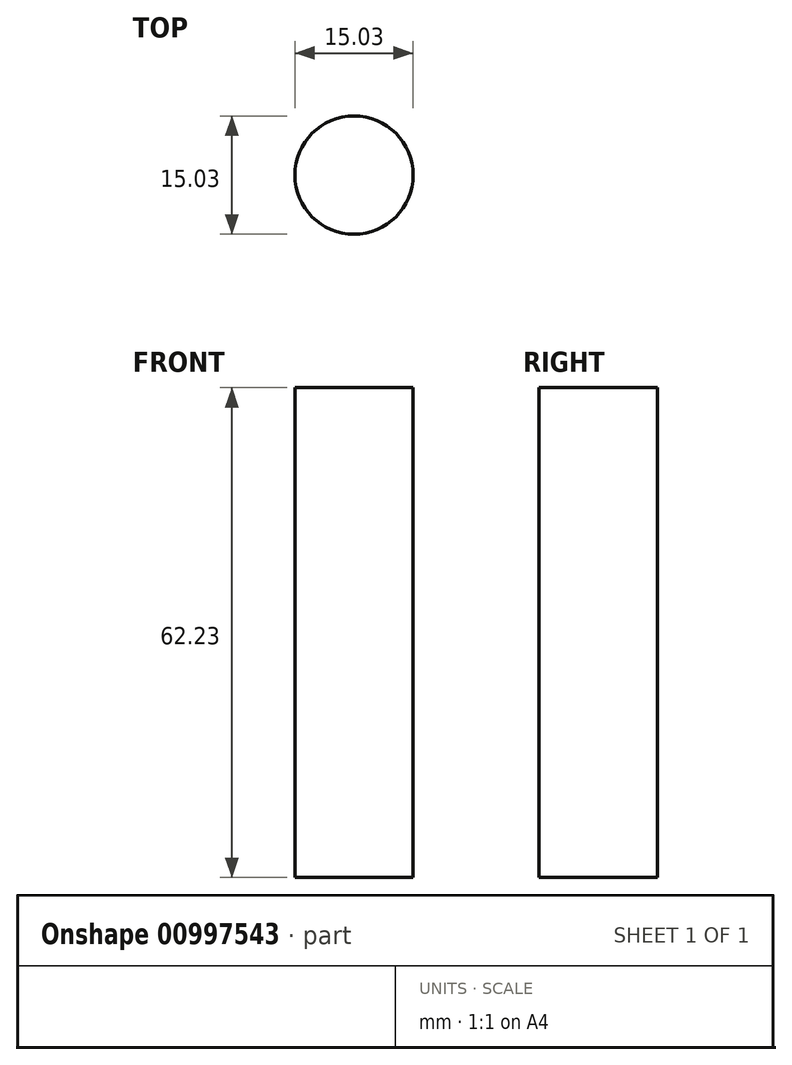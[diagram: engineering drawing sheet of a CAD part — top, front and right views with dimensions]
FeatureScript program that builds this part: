
annotation { "Feature Type Name" : "Feature", "Feature Type Description" : "" }
export const myFeature = defineFeature(function(context is Context, id is Id, definition is map)
    precondition{}
    {
        {
            var Q0;
            Q0=qCreatedBy(makeId("Top.planeOp"),FACE);
            var sketch = newSketch(context, id + "F0", { "sketchPlane" : qUnion([Q0])});
            skCircle(sketch, "E0", {"center": v(0, 0) * mm, "radius": 67.2 * mm});
            skCircle(sketch, "E1", {"center": v(-55.37, -38.06) * mm, "radius": 7.51 * mm});
            skSolve(sketch);
        }
        {
            var Q0;
            {var subQ0=sQuery(id+"F0.wireOp",EDGE,"E1");var subQ1=sQuery(id+"F0.wireOp",EDGE,"E0");var subQ2=makeQuery(id+"F0.imprint","INTERSECT",VERTEX,{"disambiguationData":[OD(0.0)],"derivedFrom":[subQ1,subQ0]});Q0=makeQuery(id+"F0.imprint","IMPRINT",FACE,{"disambiguationData":[TD([[makeQuery(id+"F0.imprint","IMPRINT",EDGE,{"disambiguationData":[TD([[subQ2,-1.0]])],"derivedFrom":subQ1}),1.0]])]});}
            var Q1;
            {var subQ0=sQuery(id+"F0.wireOp",EDGE,"E1");var subQ1=sQuery(id+"F0.wireOp",EDGE,"E0");var subQ2=makeQuery(id+"F0.imprint","INTERSECT",VERTEX,{"disambiguationData":[OD(0.0)],"derivedFrom":[subQ1,subQ0]});Q1=makeQuery(id+"F0.imprint","IMPRINT",FACE,{"disambiguationData":[TD([[makeQuery(id+"F0.imprint","IMPRINT",EDGE,{"disambiguationData":[TD([[subQ2,-1.0]])],"derivedFrom":subQ1}),-1.0]])]});}
            extrude(context, id + "F1", {"entities" : qUnion([Q0, Q1]), "depth" : 62.23 * mm, "offsetDistance" : 25.4 * mm});
        }
    });
